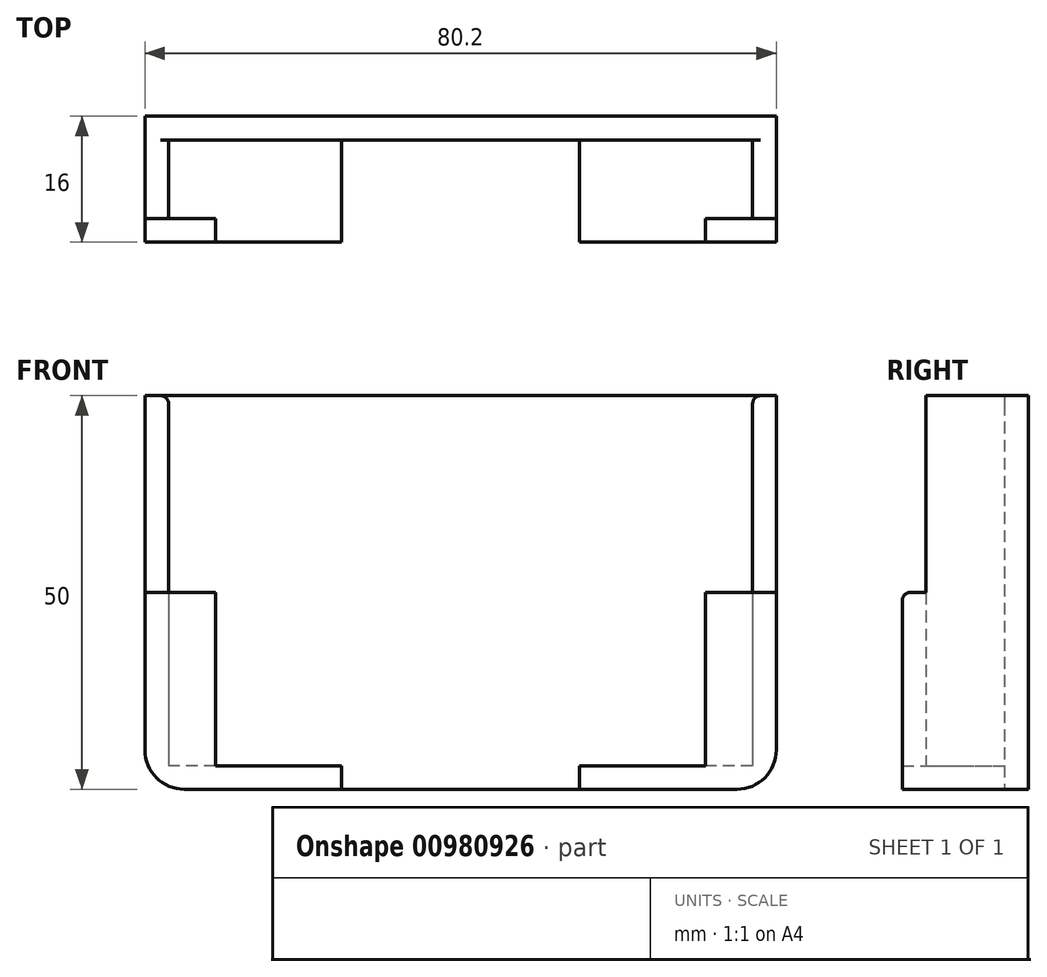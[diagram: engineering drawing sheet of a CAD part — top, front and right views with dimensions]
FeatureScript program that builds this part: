
annotation { "Feature Type Name" : "Feature", "Feature Type Description" : "" }
export const myFeature = defineFeature(function(context is Context, id is Id, definition is map)
    precondition{}
    {
        {
            var Q0;
            Q0=qCreatedBy(makeId("Front.planeOp"),FACE);
            var sketch = newSketch(context, id + "F0", { "sketchPlane" : qUnion([Q0])});
            skLineSegment(sketch, "E0.bottom", {"start": v(-40.1, 50) * mm, "end": v(40.1, 50) * mm});
            skLineSegment(sketch, "E0.top", {"start": v(-40.1, 0) * mm, "end": v(40.1, 0) * mm});
            skLineSegment(sketch, "E0.left", {"start": v(-40.1, 50) * mm, "end": v(-40.1, 0) * mm});
            skLineSegment(sketch, "E0.right", {"start": v(40.1, 50) * mm, "end": v(40.1, 0) * mm});
            skPoint(sketch, "E1", {"position": v(0, 0) * mm});
            skSolve(sketch);
        }
        {
            var Q0;
            Q0 = qSketchRegion(id + "F0", true);
            extrude(context, id + "F1", {"entities" : qUnion([Q0]), "depth" : 3 * mm, "offsetDistance" : 25 * mm});
        }
        {
            var Q0;
            Q0=makeQuery(id+"F1.opExtrude","CAP_FACE",FACE,{"disambiguationData":[OSD([sQuery(id+"F0.wireOp",EDGE,"E0.bottom"),sQuery(id+"F0.wireOp",EDGE,"E0.top"),sQuery(id+"F0.wireOp",EDGE,"E0.left"),sQuery(id+"F0.wireOp",EDGE,"E0.right")])],"isStart":false});
            var sketch = newSketch(context, id + "F2", { "sketchPlane" : qUnion([Q0])});
            skLineSegment(sketch, "E2", {"start": v(-37.1, 50) * mm, "end": v(-37.1, 0) * mm});
            skLineSegment(sketch, "E3", {"start": v(37.1, 50) * mm, "end": v(37.1, 0) * mm});
            skLineSegment(sketch, "E4", {"start": v(40.1, 3) * mm, "end": v(-40.1, 3) * mm});
            skLineSegment(sketch, "E5", {"start": v(-15.1, 3) * mm, "end": v(-15.1, 0) * mm});
            skLineSegment(sketch, "E6", {"start": v(15.1, 3) * mm, "end": v(15.1, 0) * mm});
            skSolve(sketch);
        }
        {
            var Q0;
            Q0 = qSketchRegion(id + "F2", true);
            var Q1;
            {var subQ0=sQuery(id+"F2.wireOp",EDGE,"E2");var subQ1=makeQuery(id+"F1.opExtrude","CAP_EDGE",EDGE,{"disambiguationData":[OSD([sQuery(id+"F0.wireOp",EDGE,"E0.bottom")])],"isStart":false});var subQ2=makeQuery(id+"F2.imprint","INTERSECT",VERTEX,{"derivedFrom":[subQ1,subQ0]});Q1=makeQuery(id+"F2.imprint","IMPRINT",FACE,{"disambiguationData":[TD([[makeQuery(id+"F2.imprint","IMPRINT",EDGE,{"disambiguationData":[TD([[subQ2,-1.0]])],"derivedFrom":subQ0}),-1.0]])]});}
            var Q2;
            {var subQ0=sQuery(id+"F2.wireOp",EDGE,"E2");var subQ1=makeQuery(id+"F1.opExtrude","CAP_EDGE",EDGE,{"disambiguationData":[OSD([sQuery(id+"F0.wireOp",EDGE,"E0.top")])],"isStart":false});var subQ2=makeQuery(id+"F2.imprint","INTERSECT",VERTEX,{"derivedFrom":[subQ1,subQ0]});Q2=makeQuery(id+"F2.imprint","IMPRINT",FACE,{"disambiguationData":[TD([[makeQuery(id+"F2.imprint","IMPRINT",EDGE,{"disambiguationData":[TD([[subQ2,1.0]])],"derivedFrom":subQ0}),-1.0]])]});}
            var Q3;
            {var subQ5=sQuery(id+"F2.wireOp",EDGE,"E5");Q3=makeQuery(id+"F2.imprint","IMPRINT",FACE,{"disambiguationData":[TD([[makeQuery(id+"F2.imprint","IMPRINT",EDGE,{"derivedFrom":subQ5}),-1.0]])]});}
            var Q4;
            {var subQ5=sQuery(id+"F2.wireOp",EDGE,"E6");Q4=makeQuery(id+"F2.imprint","IMPRINT",FACE,{"disambiguationData":[TD([[makeQuery(id+"F2.imprint","IMPRINT",EDGE,{"derivedFrom":subQ5}),1.0]])]});}
            var Q5;
            {var subQ0=sQuery(id+"F2.wireOp",EDGE,"E3");var subQ1=makeQuery(id+"F1.opExtrude","CAP_EDGE",EDGE,{"disambiguationData":[OSD([sQuery(id+"F0.wireOp",EDGE,"E0.top")])],"isStart":false});var subQ2=makeQuery(id+"F2.imprint","INTERSECT",VERTEX,{"derivedFrom":[subQ1,subQ0]});Q5=makeQuery(id+"F2.imprint","IMPRINT",FACE,{"disambiguationData":[TD([[makeQuery(id+"F2.imprint","IMPRINT",EDGE,{"disambiguationData":[TD([[subQ2,1.0]])],"derivedFrom":subQ0}),1.0]])]});}
            var Q6;
            {var subQ0=sQuery(id+"F2.wireOp",EDGE,"E3");var subQ1=makeQuery(id+"F1.opExtrude","CAP_EDGE",EDGE,{"disambiguationData":[OSD([sQuery(id+"F0.wireOp",EDGE,"E0.bottom")])],"isStart":false});var subQ2=makeQuery(id+"F2.imprint","INTERSECT",VERTEX,{"derivedFrom":[subQ1,subQ0]});Q6=makeQuery(id+"F2.imprint","IMPRINT",FACE,{"disambiguationData":[TD([[makeQuery(id+"F2.imprint","IMPRINT",EDGE,{"disambiguationData":[TD([[subQ2,-1.0]])],"derivedFrom":subQ0}),1.0]])]});}
            extrude(context, id + "F3", {"entities" : qUnion([Q0, Q1, Q2, Q3, Q4, Q5, Q6]), "operationType" : NewBodyOperationType.ADD, "depth" : 10 * mm, "offsetDistance" : 25 * mm});
        }
        {
            var Q0;
            Q0=makeQuery(id+"F3.opExtrude","CAP_FACE",FACE,{"disambiguationData":[OSD([sQuery(id+"F0.wireOp",EDGE,"E0.bottom"),sQuery(id+"F0.wireOp",EDGE,"E0.top"),sQuery(id+"F0.wireOp",EDGE,"E0.left"),sQuery(id+"F2.wireOp",EDGE,"E2"),sQuery(id+"F2.wireOp",EDGE,"E4"),sQuery(id+"F2.wireOp",EDGE,"E5")])],"isStart":false});
            var sketch = newSketch(context, id + "F4", { "sketchPlane" : qUnion([Q0])});
            skLineSegment(sketch, "E7.bottom", {"start": v(-40.1, 0) * mm, "end": v(-31.1, 0) * mm});
            skLineSegment(sketch, "E7.top", {"start": v(-40.1, 25) * mm, "end": v(-31.1, 25) * mm});
            skLineSegment(sketch, "E7.left", {"start": v(-40.1, 0) * mm, "end": v(-40.1, 25) * mm});
            skLineSegment(sketch, "E7.right", {"start": v(-31.1, 0) * mm, "end": v(-31.1, 25) * mm});
            skLineSegment(sketch, "E8.0.0", {"start": v(37.1, 3) * mm, "end": v(15.1, 3) * mm});
            skLineSegment(sketch, "E8.0.1", {"start": v(15.1, 3) * mm, "end": v(15.1, 0) * mm});
            skLineSegment(sketch, "E8.0.2", {"start": v(15.1, 0) * mm, "end": v(40.1, 0) * mm});
            skLineSegment(sketch, "E8.0.3", {"start": v(40.1, 0) * mm, "end": v(40.1, 50) * mm});
            skLineSegment(sketch, "E8.0.4", {"start": v(40.1, 50) * mm, "end": v(37.1, 50) * mm});
            skLineSegment(sketch, "E8.0.5", {"start": v(37.1, 50) * mm, "end": v(37.1, 3) * mm});
            skLineSegment(sketch, "E9.bottom", {"start": v(40.1, 0) * mm, "end": v(31.1, 0) * mm});
            skLineSegment(sketch, "E9.top", {"start": v(40.1, 25) * mm, "end": v(31.1, 25) * mm});
            skLineSegment(sketch, "E9.left", {"start": v(40.1, 0) * mm, "end": v(40.1, 25) * mm});
            skLineSegment(sketch, "E9.right", {"start": v(31.1, 0) * mm, "end": v(31.1, 25) * mm});
            skSolve(sketch);
        }
        {
            var Q0;
            {var subQ0=sQuery(id+"F4.wireOp",EDGE,"E9.right");var subQ1=sQuery(id+"F4.wireOp",EDGE,"E8.0.0");var subQ2=makeQuery(id+"F4.imprint","INTERSECT",VERTEX,{"derivedFrom":[subQ1,subQ0]});Q0=makeQuery(id+"F4.imprint","IMPRINT",FACE,{"disambiguationData":[TD([[makeQuery(id+"F4.imprint","IMPRINT",EDGE,{"disambiguationData":[TD([[subQ2,1.0]])],"derivedFrom":subQ1}),-1.0]])]});}
            var Q1;
            {var subQ3=sQuery(id+"F4.wireOp",EDGE,"E8.0.1");Q1=makeQuery(id+"F4.imprint","IMPRINT",FACE,{"disambiguationData":[TD([[makeQuery(id+"F4.imprint","IMPRINT",EDGE,{"derivedFrom":subQ3}),1.0]])]});}
            var Q2;
            {var subQ6=sQuery(id+"F4.wireOp",EDGE,"E8.0.0");var subQ9=sQuery(id+"F4.wireOp",EDGE,"E9.right");var subQ11=makeQuery(id+"F4.imprint","INTERSECT",VERTEX,{"derivedFrom":[subQ6,subQ9]});Q2=makeQuery(id+"F4.imprint","IMPRINT",FACE,{"disambiguationData":[TD([[makeQuery(id+"F4.imprint","IMPRINT",EDGE,{"disambiguationData":[TD([[subQ11,1.0]])],"derivedFrom":subQ6}),1.0]])]});}
            var Q3;
            {var subQ0=sQuery(id+"F4.wireOp",EDGE,"E7.right");var subQ1=sQuery(id+"F4.wireOp",EDGE,"E7.top");var subQ2=makeQuery(id+"F4.imprint","INTERSECT",VERTEX,{"derivedFrom":[subQ1,subQ0]});Q3=makeQuery(id+"F4.imprint","IMPRINT",FACE,{"disambiguationData":[TD([[makeQuery(id+"F4.imprint","IMPRINT",EDGE,{"disambiguationData":[TD([[subQ2,1.0]])],"derivedFrom":subQ1}),-1.0]])]});}
            var Q4;
            {var subQ1=sQuery(id+"F4.wireOp",EDGE,"E7.bottom");Q4=makeQuery(id+"F4.imprint","IMPRINT",FACE,{"disambiguationData":[TD([[makeQuery(id+"F4.imprint","IMPRINT",EDGE,{"derivedFrom":subQ1}),1.0]])]});}
            var Q5;
            {var subQ5=sQuery(id+"F2.wireOp",EDGE,"E5");var subQ11=makeQuery(id+"F3.opExtrude","CAP_EDGE",EDGE,{"disambiguationData":[OSD([subQ5])],"isStart":false});Q5=makeQuery(id+"F4.imprint","IMPRINT",FACE,{"disambiguationData":[TD([[makeQuery(id+"F4.imprint","IMPRINT",EDGE,{"derivedFrom":subQ11}),-1.0]])]});}
            extrude(context, id + "F5", {"entities" : qUnion([Q0, Q1, Q2, Q3, Q4, Q5]), "operationType" : NewBodyOperationType.ADD, "depth" : 3 * mm, "offsetDistance" : 25 * mm});
        }
        {
            var Q0;
            {var subQ0=sQuery(id+"F0.wireOp",EDGE,"E0.right");var subQ1=sQuery(id+"F0.wireOp",EDGE,"E0.top");Q0=makeQuery(id+"F5.boolean.opBoolean","MERGE",EDGE,{"derivedFrom":[makeQuery(id+"F3.boolean.opBoolean","MERGE",EDGE,{"derivedFrom":[makeQuery(id+"F1.opExtrude","SWEPT_EDGE",EDGE,{"disambiguationData":[OSD([subQ1,subQ0])]}),makeQuery(id+"F3.opExtrude","SWEPT_EDGE",EDGE,{"disambiguationData":[OSD([subQ1,subQ0])]})]}),makeQuery(id+"F5.opExtrude","SWEPT_EDGE",EDGE,{"disambiguationData":[OSD([sQuery(id+"F4.wireOp",EDGE,"E8.0.2"),sQuery(id+"F4.wireOp",EDGE,"E8.0.3")])]})]});}
            var Q1;
            {var subQ0=sQuery(id+"F0.wireOp",EDGE,"E0.left");var subQ1=sQuery(id+"F0.wireOp",EDGE,"E0.top");Q1=makeQuery(id+"F5.boolean.opBoolean","MERGE",EDGE,{"derivedFrom":[makeQuery(id+"F3.boolean.opBoolean","MERGE",EDGE,{"derivedFrom":[makeQuery(id+"F1.opExtrude","SWEPT_EDGE",EDGE,{"disambiguationData":[OSD([subQ1,subQ0])]}),makeQuery(id+"F3.opExtrude","SWEPT_EDGE",EDGE,{"disambiguationData":[OSD([subQ1,subQ0])]})]}),makeQuery(id+"F5.opExtrude","SWEPT_EDGE",EDGE,{"disambiguationData":[OSD([sQuery(id+"F4.wireOp",EDGE,"E7.bottom"),sQuery(id+"F4.wireOp",EDGE,"E7.left")])]})]});}
            fillet(context, id + "F6", {"entities" : qUnion([Q0, Q1]), "radius" : 5 * mm, "tangentPropagation" : true, "allowEdgeOverflow" : false});
        }
        {
            var Q0;
            Q0=makeQuery(id+"F5.opExtrude","CAP_EDGE",EDGE,{"disambiguationData":[OSD([sQuery(id+"F4.wireOp",EDGE,"E7.top")])],"isStart":false});
            var Q1;
            Q1=makeQuery(id+"F5.opExtrude","CAP_EDGE",EDGE,{"disambiguationData":[OSD([sQuery(id+"F4.wireOp",EDGE,"E9.top")])],"isStart":false});
            var Q2;
            Q2=makeQuery(id+"F3.opExtrude","SWEPT_EDGE",EDGE,{"disambiguationData":[OSD([sQuery(id+"F0.wireOp",EDGE,"E0.bottom"),sQuery(id+"F2.wireOp",EDGE,"E2")])]});
            var Q3;
            Q3=makeQuery(id+"F3.opExtrude","SWEPT_EDGE",EDGE,{"disambiguationData":[OSD([sQuery(id+"F0.wireOp",EDGE,"E0.bottom"),sQuery(id+"F2.wireOp",EDGE,"E3")])]});
            fillet(context, id + "F7", {"entities" : qUnion([Q0, Q1, Q2, Q3]), "radius" : 1 * mm, "tangentPropagation" : true, "allowEdgeOverflow" : false});
        }
    });
